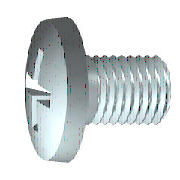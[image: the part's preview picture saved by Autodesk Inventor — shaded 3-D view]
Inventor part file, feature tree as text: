
AUTODESK INVENTOR PART (.ipt)
format: ipt  version: 2021 (Build 250183000, 183)  size: 250,880 bytes
history: native  units: mm (DEFAULTED — no unit token found)
features: chamfer x4, other x3, sketch x2, revolve x1, fillet x1, extrude x1, pattern_circular x1
ambient origin geometry x8: Origin, YZ Plane, XZ Plane, XY Plane, X Axis, Y Axis, Z Axis, Center Point
bodies: Solid1 (feature_tree)
feature tree (13):
  revolve  "Revolution1"  [1 undecoded]
  chamfer  "Chamfer1"  Distance=0.125mm
  chamfer  "Chamfer2"  Distance=0.125mm
  fillet  "Fillet1"  Radius=0.25mm
  extrude  "Extrusion1"  Depth=10.0mm
  pattern_circular  "PolarArray1"  [2 undecoded]
  chamfer  "Chamfer3"  Distance=1.612mm
  chamfer  "Chamfer4"  Distance=0.62mm
  other  "MSC_A1"
  other  "MSC_PF1"
  other  "MSC_PT1"
  sketch  "Sketch2"  dims[d6=2.75mm d9=0.872665mm]
  sketch  "Sketch3"  dims[d10=90.0deg d11=0.125mm d12=0.125mm d13=0.25mm d14=0.25mm d16=10.0mm d17=0.0mm d19=1.612mm d20=0.62mm d21=2.52mm d22=0.516667mm d23=0.0mm d24=40.0mm d26=360.0deg d28=0.0mm d29=0.0mm d30=0.442857mm d31=0.442857mm d32=0.206667mm d33=0.206667mm d34=45.0deg d35=45.0deg d36=45.0deg d37=45.0deg d38=0.0mm d39=0.0mm d40=0.0mm]
note: 3 required parameter values undecoded (feature->parameter linkage not recoverable at this tier; creation-order binding heuristic only, values carry confidence <= 0.55)